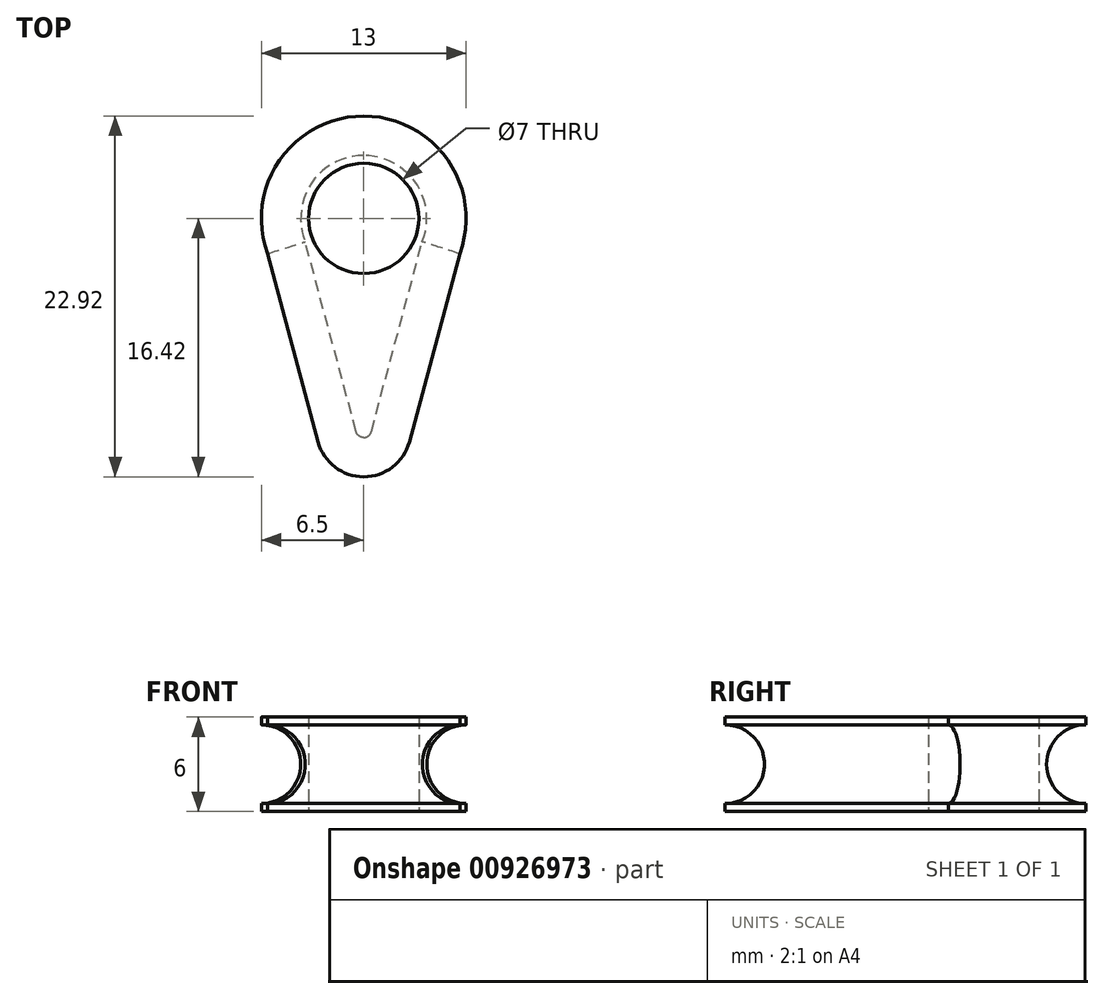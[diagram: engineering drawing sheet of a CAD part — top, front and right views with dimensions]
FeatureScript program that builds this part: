
annotation { "Feature Type Name" : "Feature", "Feature Type Description" : "" }
export const myFeature = defineFeature(function(context is Context, id is Id, definition is map)
    precondition{}
    {
        {
            var Q0;
            Q0=qCreatedBy(makeId("Top.planeOp"),FACE);
            var sketch = newSketch(context, id + "F0", { "sketchPlane" : qUnion([Q0])});
            skLineSegment(sketch, "E0", {"start": v(0, 71.12) * mm, "end": v(0, 6.5) * mm});
            skArc(sketch, "E1", {"start": v(0, 3.5) * mm, "mid": v(-3.5, 0) * mm, "end": v(0, -3.5) * mm});
            skArc(sketch, "E2", {"start": v(0, 6.5) * mm, "mid": v(-5.33, 3.72) * mm, "end": v(-6.1, -2.24) * mm});
            skLineSegment(sketch, "E3", {"start": v(-6.1, -2.24) * mm, "end": v(-2.9, -14.2) * mm});
            skArc(sketch, "E4.filletArc", {"start": v(-2.9, -14.2) * mm, "mid": v(-1.83, -15.8) * mm, "end": v(0, -16.42) * mm});
            skLineSegment(sketch, "E5", {"start": v(0, -16.35) * mm, "end": v(0, -85.72) * mm});
            skLineSegment(sketch, "E6", {"start": v(0, 6.5) * mm, "end": v(0, -16.42) * mm});
            skSolve(sketch);
        }
        {
            var Q0;
            {var subQ1=sQuery(id+"F0.wireOp",EDGE,"E2");Q0=makeQuery(id+"F0.imprint","IMPRINT",FACE,{"disambiguationData":[TD([[makeQuery(id+"F0.imprint","IMPRINT",EDGE,{"derivedFrom":subQ1}),1.0]])]});}
            extrude(context, id + "F1", {"entities" : qUnion([Q0]), "depth" : 6 * mm, "offsetDistance" : 25 * mm});
        }
        {
            var Q0;
            Q0=makeQuery(id+"F1.opExtrude","SWEPT_EDGE",EDGE,{"disambiguationData":[OSD([sQuery(id+"F0.wireOp",EDGE,"E3"),sQuery(id+"F0.wireOp",EDGE,"E4.filletArc")])]});
            cPlane(context, id + "F2", {"entities" : qUnion([Q0]), "cplaneType" : CPlaneType.LINE_ANGLE, "offset" : 25 * mm, "angle" : 75 * degree, "width" : 150 * mm, "height" : 150 * mm});
        }
        {
            var Q0;
            Q0=qCreatedBy(id+"F2.planeOp",FACE);
            var sketch = newSketch(context, id + "F3", { "sketchPlane" : qUnion([Q0])});
            skLineSegment(sketch, "E7.0", {"start": v(6.47, 5.5) * mm, "end": v(6.47, 0.5) * mm});
            skArc(sketch, "E8", {"start": v(6.47, 5.5) * mm, "mid": v(3.97, 3) * mm, "end": v(6.47, 0.5) * mm});
            skPoint(sketch, "E9.orphan", {"position": v(6.47, 6) * mm});
            skPoint(sketch, "E10.orphan", {"position": v(6.47, 0) * mm});
            skSolve(sketch);
        }
        {
            var Q0;
            Q0 = qSketchRegion(id + "F3", true);
            var Q1;
            Q1=makeQuery(id+"F1.opExtrude","CAP_EDGE",EDGE,{"disambiguationData":[OSD([sQuery(id+"F0.wireOp",EDGE,"E3")])],"isStart":true});
            var Q2;
            Q2=makeQuery(id+"F1.opExtrude","CAP_EDGE",EDGE,{"disambiguationData":[OSD([sQuery(id+"F0.wireOp",EDGE,"E4.filletArc")])],"isStart":true});
            var Q3;
            Q3=makeQuery(id+"F1.opExtrude","CAP_EDGE",EDGE,{"disambiguationData":[OSD([sQuery(id+"F0.wireOp",EDGE,"E2")])],"isStart":true});
            sweep(context, id + "F4", {"operationType" : NewBodyOperationType.REMOVE, "profiles" : qUnion([Q0]), "path" : qUnion([Q1, Q2, Q3])});
        }
        {
            var Q0;
            Q0=makeQuery(id+"F1.opExtrude","SWEPT_BODY",BODY,{"disambiguationData":[OSD([sQuery(id+"F0.wireOp",EDGE,"E1"),sQuery(id+"F0.wireOp",EDGE,"E2"),sQuery(id+"F0.wireOp",EDGE,"E3"),sQuery(id+"F0.wireOp",EDGE,"E4.filletArc"),sQuery(id+"F0.wireOp",EDGE,"E6")])]});
            var Q1;
            Q1=qCreatedBy(makeId("Right.planeOp"),FACE);
            mirror(context, id + "F5", {"operationType" : NewBodyOperationType.ADD, "entities" : qUnion([Q0]), "mirrorPlane" : qUnion([Q1])});
        }
    });
